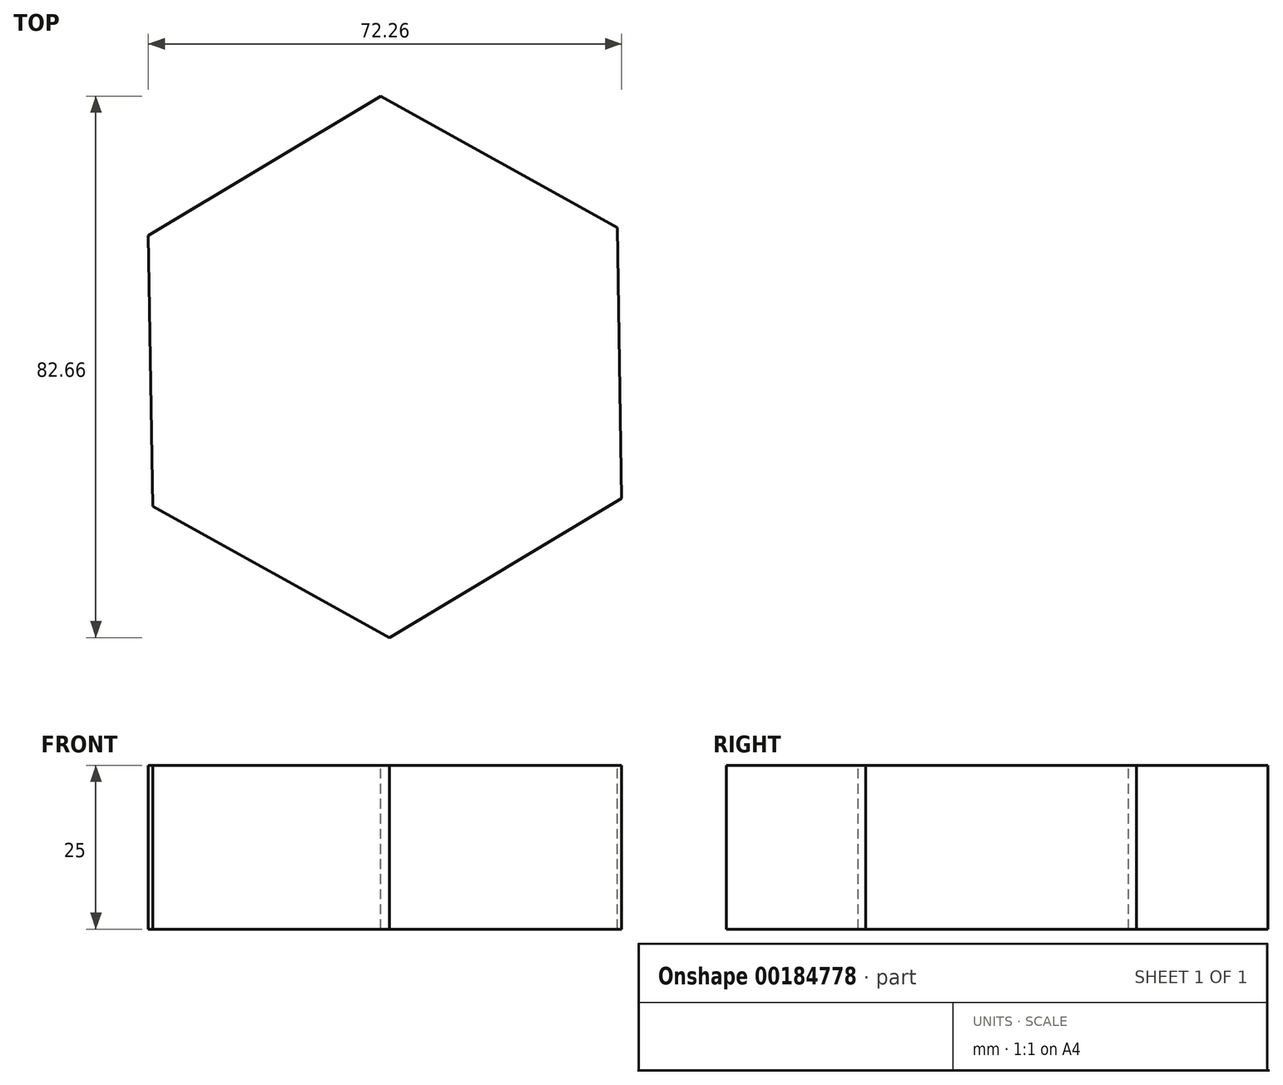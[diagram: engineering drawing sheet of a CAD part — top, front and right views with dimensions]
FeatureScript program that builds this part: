
annotation { "Feature Type Name" : "Feature", "Feature Type Description" : "" }
export const myFeature = defineFeature(function(context is Context, id is Id, definition is map)
    precondition{}
    {
        {
            var Q0;
            Q0=qCreatedBy(makeId("Top.planeOp"),FACE);
            var sketch = newSketch(context, id + "F0", { "sketchPlane" : qUnion([Q0])});
            skCircle(sketch, "E0.cCircle", {"center": v(0, 0) * mm, "radius": 41.33 * mm, "construction": true});
            skLineSegment(sketch, "E0.0", {"start": v(-35.45, -21.25) * mm, "end": v(-36.13, 20.08) * mm});
            skLineSegment(sketch, "E0.1", {"start": v(-36.13, 20.08) * mm, "end": v(-0.67, 41.33) * mm});
            skLineSegment(sketch, "E0.2", {"start": v(-0.67, 41.33) * mm, "end": v(35.45, 21.25) * mm});
            skLineSegment(sketch, "E0.3", {"start": v(35.45, 21.25) * mm, "end": v(36.13, -20.08) * mm});
            skLineSegment(sketch, "E0.4", {"start": v(36.13, -20.08) * mm, "end": v(0.67, -41.33) * mm});
            skLineSegment(sketch, "E0.5", {"start": v(0.67, -41.33) * mm, "end": v(-35.45, -21.25) * mm});
            skText(sketch, "E1", { "text": "LJ", "fontName": "DroidSansMono.ttf"});
            const initialGuessF0  = {"E1": [-0.0216, -0.01352, 1, 0, 0.02523]};
            skSetInitialGuess(sketch, initialGuessF0);
            skSolve(sketch);
        }
        {
            var Q0;
            Q0=sQuery(id+"F0.wireOp",EDGE,"E0.1");
            var Q1;
            Q1=sQuery(id+"F0.wireOp",EDGE,"E0.2");
            var Q2;
            Q2=sQuery(id+"F0.wireOp",EDGE,"E0.3");
            var Q3;
            Q3=sQuery(id+"F0.wireOp",EDGE,"E0.4");
            var Q4;
            Q4=sQuery(id+"F0.wireOp",EDGE,"E0.5");
            var Q5;
            Q5=sQuery(id+"F0.wireOp",EDGE,"E0.0");
            extrude(context, id + "F1", {"bodyType" : ToolBodyType.SURFACE, "surfaceEntities" : qUnion([Q0, Q1, Q2, Q3, Q4, Q5]), "depth" : 25 * mm});
        }
    });
